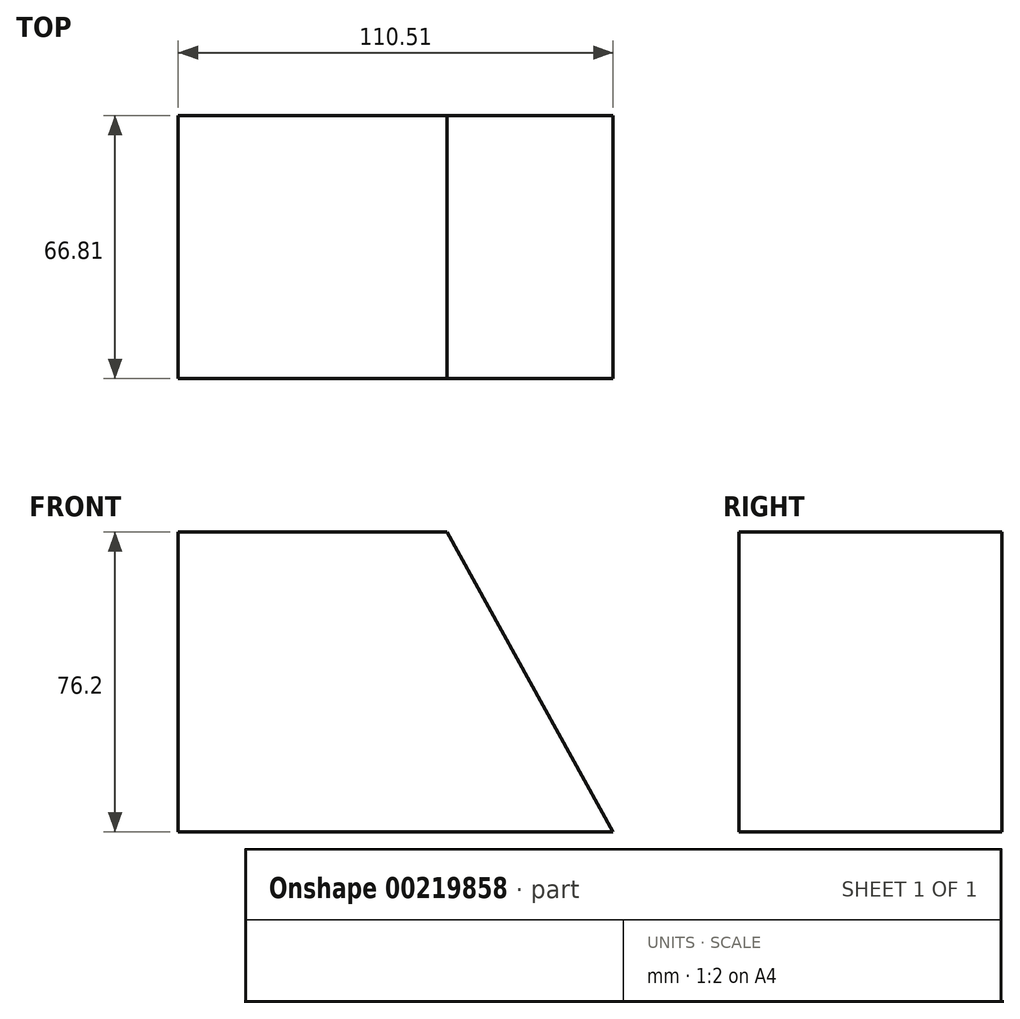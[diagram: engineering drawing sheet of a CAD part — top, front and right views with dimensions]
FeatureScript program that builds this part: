
annotation { "Feature Type Name" : "Feature", "Feature Type Description" : "" }
export const myFeature = defineFeature(function(context is Context, id is Id, definition is map)
    precondition{}
    {
        {
            var Q0;
            Q0=qCreatedBy(makeId("Top.planeOp"),FACE);
            var sketch = newSketch(context, id + "F0", { "sketchPlane" : qUnion([Q0])});
            skLineSegment(sketch, "E0.bottom", {"start": v(-41.35, 6.23) * mm, "end": v(69.16, 6.23) * mm});
            skLineSegment(sketch, "E0.top", {"start": v(-41.35, -60.58) * mm, "end": v(69.16, -60.58) * mm});
            skLineSegment(sketch, "E0.left", {"start": v(-41.35, 6.23) * mm, "end": v(-41.35, -60.58) * mm});
            skLineSegment(sketch, "E0.right", {"start": v(69.16, 6.23) * mm, "end": v(69.16, -60.58) * mm});
            skSolve(sketch);
        }
        {
            var Q0;
            Q0 = qSketchRegion(id + "F0", true);
            extrude(context, id + "F1", {"entities" : qUnion([Q0]), "depth" : 76.2 * mm});
        }
        {
            var Q0;
            Q0=makeQuery(id+"F1.opExtrude","SWEPT_FACE",FACE,{"disambiguationData":[OSD([sQuery(id+"F0.wireOp",EDGE,"E0.top")])]});
            var sketch = newSketch(context, id + "F2", { "sketchPlane" : qUnion([Q0])});
            skLineSegment(sketch, "E1", {"start": v(69.16, 0) * mm, "end": v(26.94, 76.2) * mm});
            skLineSegment(sketch, "E2", {"start": v(26.94, 76.2) * mm, "end": v(69.16, 76.2) * mm});
            skLineSegment(sketch, "E3", {"start": v(69.16, 76.2) * mm, "end": v(69.16, 5.74) * mm});
            skSolve(sketch);
        }
        {
            var Q0;
            {var subQ0=sQuery(id+"F2.wireOp",EDGE,"E1");Q0=makeQuery(id+"F2.imprint","IMPRINT",FACE,{"disambiguationData":[TD([[makeQuery(id+"F2.imprint","IMPRINT",EDGE,{"derivedFrom":subQ0}),-1.0]])]});}
            extrude(context, id + "F3", {"entities" : qUnion([Q0]), "operationType" : NewBodyOperationType.REMOVE, "oppositeDirection" : true, "depth" : 94.49 * mm});
        }
    });
